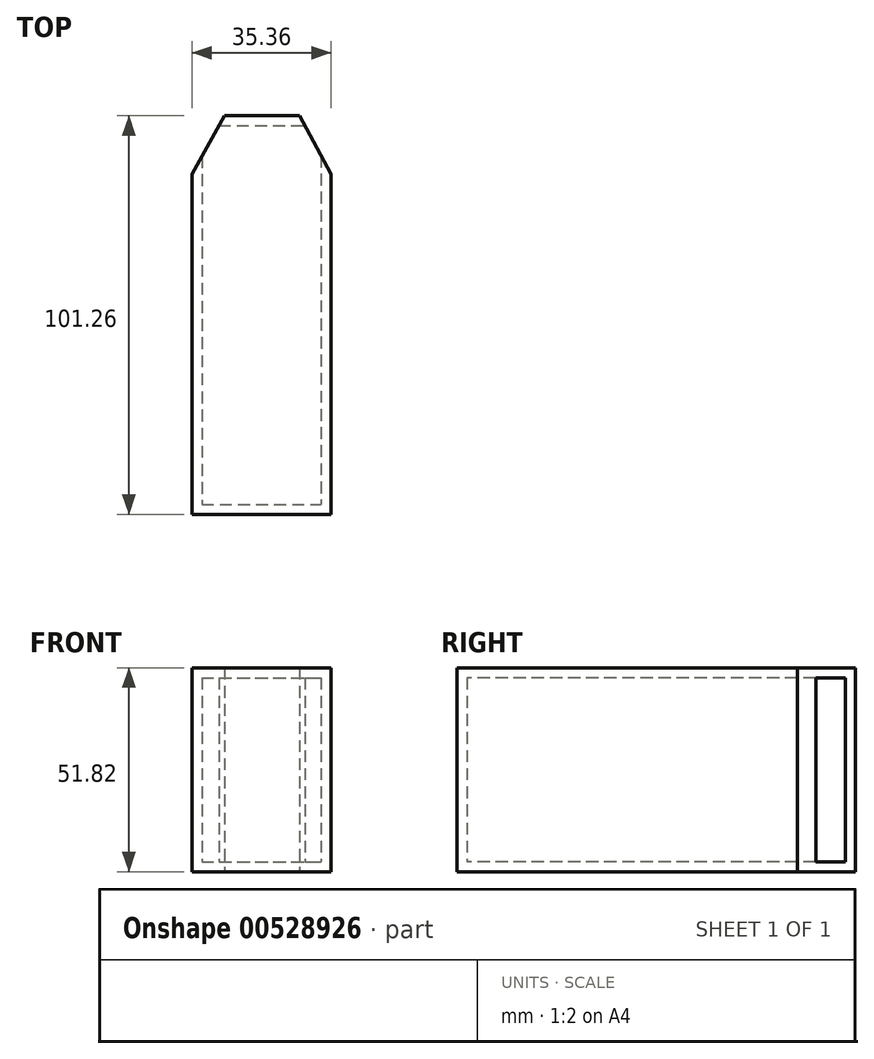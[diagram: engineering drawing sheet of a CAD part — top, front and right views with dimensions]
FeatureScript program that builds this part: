
annotation { "Feature Type Name" : "Feature", "Feature Type Description" : "" }
export const myFeature = defineFeature(function(context is Context, id is Id, definition is map)
    precondition{}
    {
        {
            var Q0;
            Q0=qCreatedBy(makeId("Top.planeOp"),FACE);
            var sketch = newSketch(context, id + "F0", { "sketchPlane" : qUnion([Q0])});
            skLineSegment(sketch, "E0.bottom", {"start": v(-17.68, 43.21) * mm, "end": v(17.68, 43.21) * mm});
            skLineSegment(sketch, "E0.top", {"start": v(-17.68, -43.21) * mm, "end": v(17.68, -43.21) * mm});
            skLineSegment(sketch, "E0.left", {"start": v(-17.68, 43.21) * mm, "end": v(-17.68, -43.21) * mm});
            skLineSegment(sketch, "E0.right", {"start": v(17.68, 43.21) * mm, "end": v(17.68, -43.21) * mm});
            skPoint(sketch, "E0.middle", {"position": v(0, 0) * mm});
            skLineSegment(sketch, "E1", {"start": v(-17.68, 43.21) * mm, "end": v(-9.41, 58.05) * mm});
            skLineSegment(sketch, "E2", {"start": v(-9.41, 58.05) * mm, "end": v(9.7, 58.05) * mm});
            skLineSegment(sketch, "E3", {"start": v(9.7, 58.05) * mm, "end": v(17.68, 43.21) * mm});
            skSolve(sketch);
        }
        {
            var Q0;
            Q0 = qSketchRegion(id + "F0", true);
            extrude(context, id + "F1", {"entities" : qUnion([Q0]), "depth" : 25.4 * mm, "offsetDistance" : 25.4 * mm, "hasSecondDirection" : true, "secondDirectionOppositeDirection" : true, "secondDirectionDepth" : 26.42 * mm});
        }
        {
            var Q0;
            Q0=makeQuery(id+"F1.opExtrude","SWEPT_FACE",FACE,{"disambiguationData":[OSD([sQuery(id+"F0.wireOp",EDGE,"E1")])]});
            var Q1;
            Q1=makeQuery(id+"F1.opExtrude","SWEPT_FACE",FACE,{"disambiguationData":[OSD([sQuery(id+"F0.wireOp",EDGE,"E3")])]});
            shell(context, id + "F2", {"entities" : qUnion([Q0, Q1]), "thickness" : 2.54 * mm});
        }
    });
